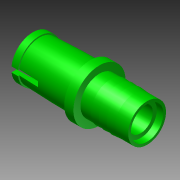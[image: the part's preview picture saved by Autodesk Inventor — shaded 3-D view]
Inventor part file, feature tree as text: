
AUTODESK INVENTOR PART (.ipt)
format: ipt  version: 2015 (Build 190159000, 159)  size: 167,424 bytes
history: native  units: in
note: dims shown in document units (in); Inventor stores cm internally (conversion verified against a paired STEP export)
features: hole x2, sketch x2, revolve x1, extrude x1
ambient origin geometry x8: Origin, YZ Plane, XZ Plane, XY Plane, X Axis, Y Axis, Z Axis, Center Point
bodies: Solid1 (feature_tree)
feature tree (6):
  revolve  "Revolution1"  [1 undecoded]
  extrude  "Extrusion1"  Depth=0.375in
  hole  "Hole1"  [1 undecoded]
  hole  "Hole2"  [1 undecoded]
  sketch  "Sketch1"  dims[d0=0.07in d1=0.4in]
  sketch  "Sketch2"  dims[d2=0.365in d3=0.29in d4=0.3in d5=0.1in d6=0.06in d7=0.33in d8=0.33in d9=0.44in d10=0.31in d11=0.05in d12=90.0deg d13=0.04in d14=0.2in d15=1.0in d16=0.0in d17=1.0in d18=1.0in d19=0.1875in d20=0.75in d21=0.25in d22=0.25in d23=0.5635in d24=0.4375in d25=0.0in d26=1.0in d27=1.0in d28=0.1875in d29=0.75in d30=0.25in d31=0.05in d32=0.5635in d33=0.375in d34=0.0in]
note: 3 required parameter values undecoded (feature->parameter linkage not recoverable at this tier; creation-order binding heuristic only, values carry confidence <= 0.55)